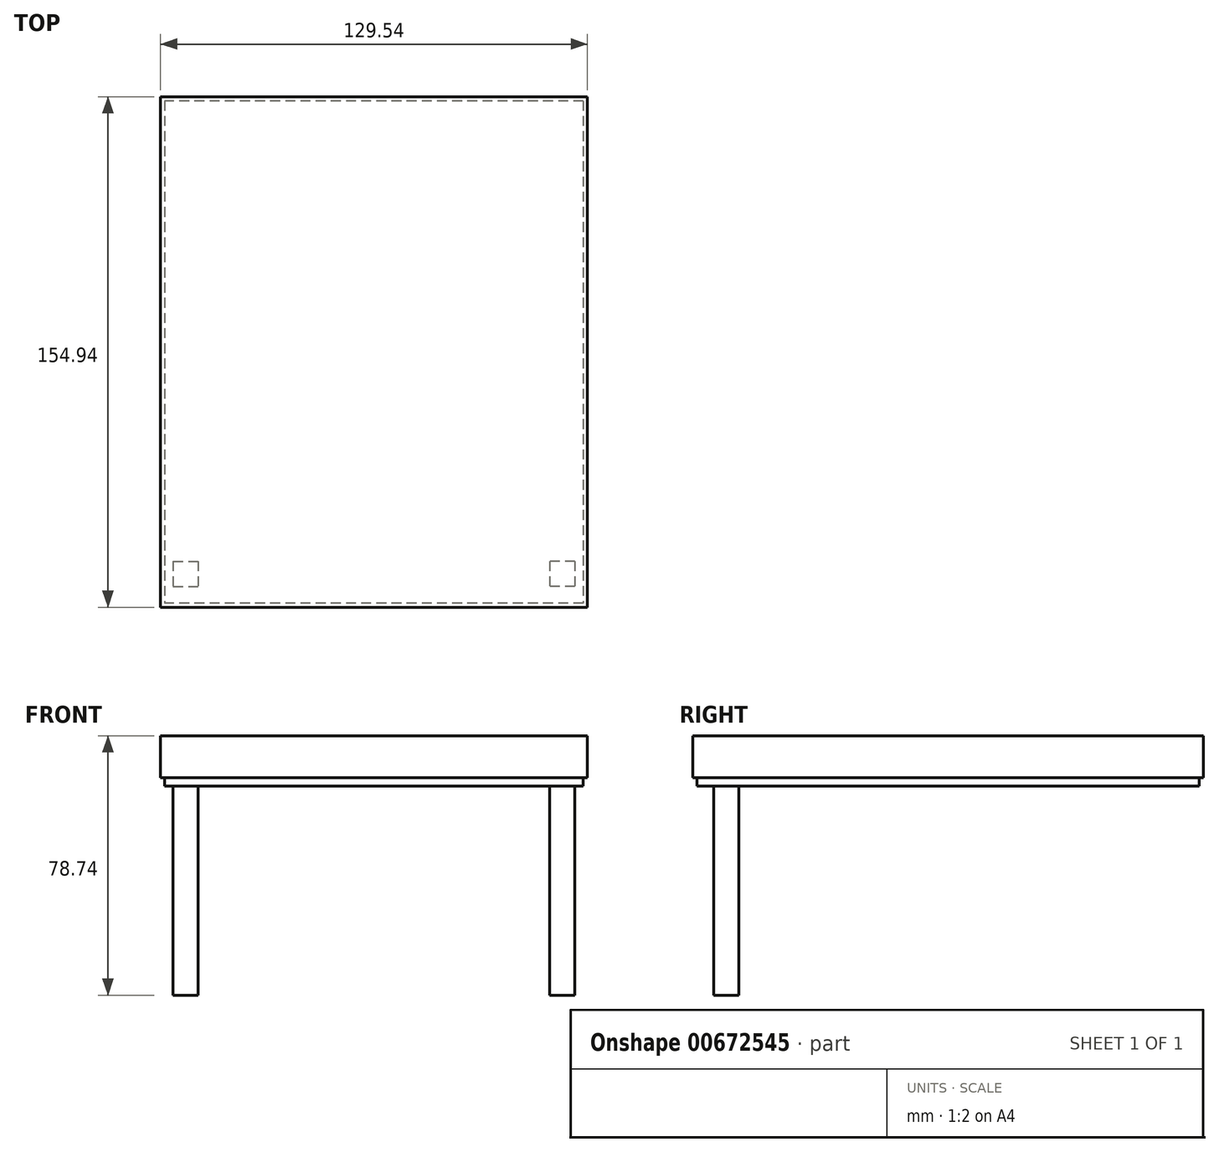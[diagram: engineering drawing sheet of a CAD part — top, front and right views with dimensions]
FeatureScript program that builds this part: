
annotation { "Feature Type Name" : "Feature", "Feature Type Description" : "" }
export const myFeature = defineFeature(function(context is Context, id is Id, definition is map)
    precondition{}
    {
        {
            var Q0;
            Q0=qCreatedBy(makeId("Top.planeOp"),FACE);
            var sketch = newSketch(context, id + "F0", { "sketchPlane" : qUnion([Q0])});
            skLineSegment(sketch, "E0.bottom", {"start": v(-60.96, -58.75) * mm, "end": v(-53.34, -58.75) * mm});
            skLineSegment(sketch, "E0.top", {"start": v(-60.96, -66.37) * mm, "end": v(-53.34, -66.37) * mm});
            skLineSegment(sketch, "E0.left", {"start": v(-60.96, -58.75) * mm, "end": v(-60.96, -66.37) * mm});
            skLineSegment(sketch, "E0.right", {"start": v(-53.34, -58.75) * mm, "end": v(-53.34, -66.37) * mm});
            skLineSegment(sketch, "E1.MirrorCS", {"start": v(60.96, -58.75) * mm, "end": v(53.34, -58.75) * mm});
            skLineSegment(sketch, "E2.MirrorCS", {"start": v(60.96, -58.75) * mm, "end": v(60.96, -66.37) * mm});
            skLineSegment(sketch, "E3.MirrorCS", {"start": v(60.96, -66.37) * mm, "end": v(53.34, -66.37) * mm});
            skLineSegment(sketch, "E4.MirrorCS", {"start": v(53.34, -58.75) * mm, "end": v(53.34, -66.37) * mm});
            skSolve(sketch);
        }
        {
            var Q0;
            Q0 = qSketchRegion(id + "F0", true);
            extrude(context, id + "F1", {"entities" : qUnion([Q0]), "depth" : 63.5 * mm, "offsetDistance" : 25.4 * mm});
        }
        {
            var Q0;
            Q0=makeQuery(id+"F1.opExtrude","CAP_FACE",FACE,{"disambiguationData":[OSD([sQuery(id+"F0.wireOp",EDGE,"E0.bottom"),sQuery(id+"F0.wireOp",EDGE,"E0.top"),sQuery(id+"F0.wireOp",EDGE,"E0.left"),sQuery(id+"F0.wireOp",EDGE,"E0.right")])],"isStart":false});
            var sketch = newSketch(context, id + "F2", { "sketchPlane" : qUnion([Q0])});
            skLineSegment(sketch, "E5.bottom", {"start": v(-63.5, -71.45) * mm, "end": v(63.5, -71.45) * mm});
            skLineSegment(sketch, "E5.top", {"start": v(-63.5, 80.95) * mm, "end": v(63.5, 80.95) * mm});
            skLineSegment(sketch, "E5.left", {"start": v(-63.5, -71.45) * mm, "end": v(-63.5, 80.95) * mm});
            skLineSegment(sketch, "E5.right", {"start": v(63.5, -71.45) * mm, "end": v(63.5, 80.95) * mm});
            skSolve(sketch);
        }
        {
            var Q0;
            Q0=makeQuery(id+"F2.imprint","IMPRINT",FACE,{"disambiguationData":[TD([[makeQuery(id+"F2.imprint","IMPRINT",EDGE,{"derivedFrom":sQuery(id+"F2.wireOp",EDGE,"E5.bottom")}),1.0]])]});
            var Q1;
            Q1=makeQuery(id+"F2.imprint","IMPRINT",FACE,{"disambiguationData":[TD([[makeQuery(id+"F2.imprint","IMPRINT",EDGE,{"derivedFrom":makeQuery(id+"F1.opExtrude","CAP_EDGE",EDGE,{"disambiguationData":[OSD([sQuery(id+"F0.wireOp",EDGE,"E0.bottom")])],"isStart":false})}),-1.0]])]});
            extrude(context, id + "F3", {"entities" : qUnion([Q0, Q1]), "depth" : 12.7 * mm, "offsetDistance" : 25.4 * mm});
        }
        {
            var Q0;
            Q0=makeQuery(id+"F3.opExtrude","CAP_FACE",FACE,{"disambiguationData":[OSD([sQuery(id+"F2.wireOp",EDGE,"E5.bottom"),sQuery(id+"F2.wireOp",EDGE,"E5.top"),sQuery(id+"F2.wireOp",EDGE,"E5.left"),sQuery(id+"F2.wireOp",EDGE,"E5.right")])],"isStart":true});
            var sketch = newSketch(context, id + "F4", { "sketchPlane" : qUnion([Q0])});
            skLineSegment(sketch, "E6.bottom", {"start": v(-64.77, 72.72) * mm, "end": v(64.77, 72.72) * mm});
            skLineSegment(sketch, "E6.top", {"start": v(-64.77, -82.22) * mm, "end": v(64.77, -82.22) * mm});
            skLineSegment(sketch, "E6.left", {"start": v(-64.77, 72.72) * mm, "end": v(-64.77, -82.22) * mm});
            skLineSegment(sketch, "E6.right", {"start": v(64.77, 72.72) * mm, "end": v(64.77, -82.22) * mm});
            skSolve(sketch);
        }
        {
            var Q0;
            Q0=makeQuery(id+"F4.imprint","IMPRINT",FACE,{"disambiguationData":[TD([[makeQuery(id+"F4.imprint","IMPRINT",EDGE,{"derivedFrom":sQuery(id+"F4.wireOp",EDGE,"E6.bottom")}),-1.0]])]});
            var Q1;
            Q1=makeQuery(id+"F4.imprint","IMPRINT",FACE,{"disambiguationData":[TD([[makeQuery(id+"F4.imprint","IMPRINT",EDGE,{"derivedFrom":makeQuery(id+"F3.opExtrude","CAP_EDGE",EDGE,{"disambiguationData":[OSD([sQuery(id+"F2.wireOp",EDGE,"E5.bottom")])],"isStart":true})}),-1.0]])]});
            extrude(context, id + "F5", {"entities" : qUnion([Q0, Q1]), "operationType" : NewBodyOperationType.ADD, "oppositeDirection" : true, "depth" : 15.24 * mm, "hasOffset" : true, "offsetDistance" : 5.08 * mm, "hasSecondDirection" : true, "secondDirectionOppositeDirection" : false, "secondDirectionDepth" : -2.54 * mm});
        }
    });
